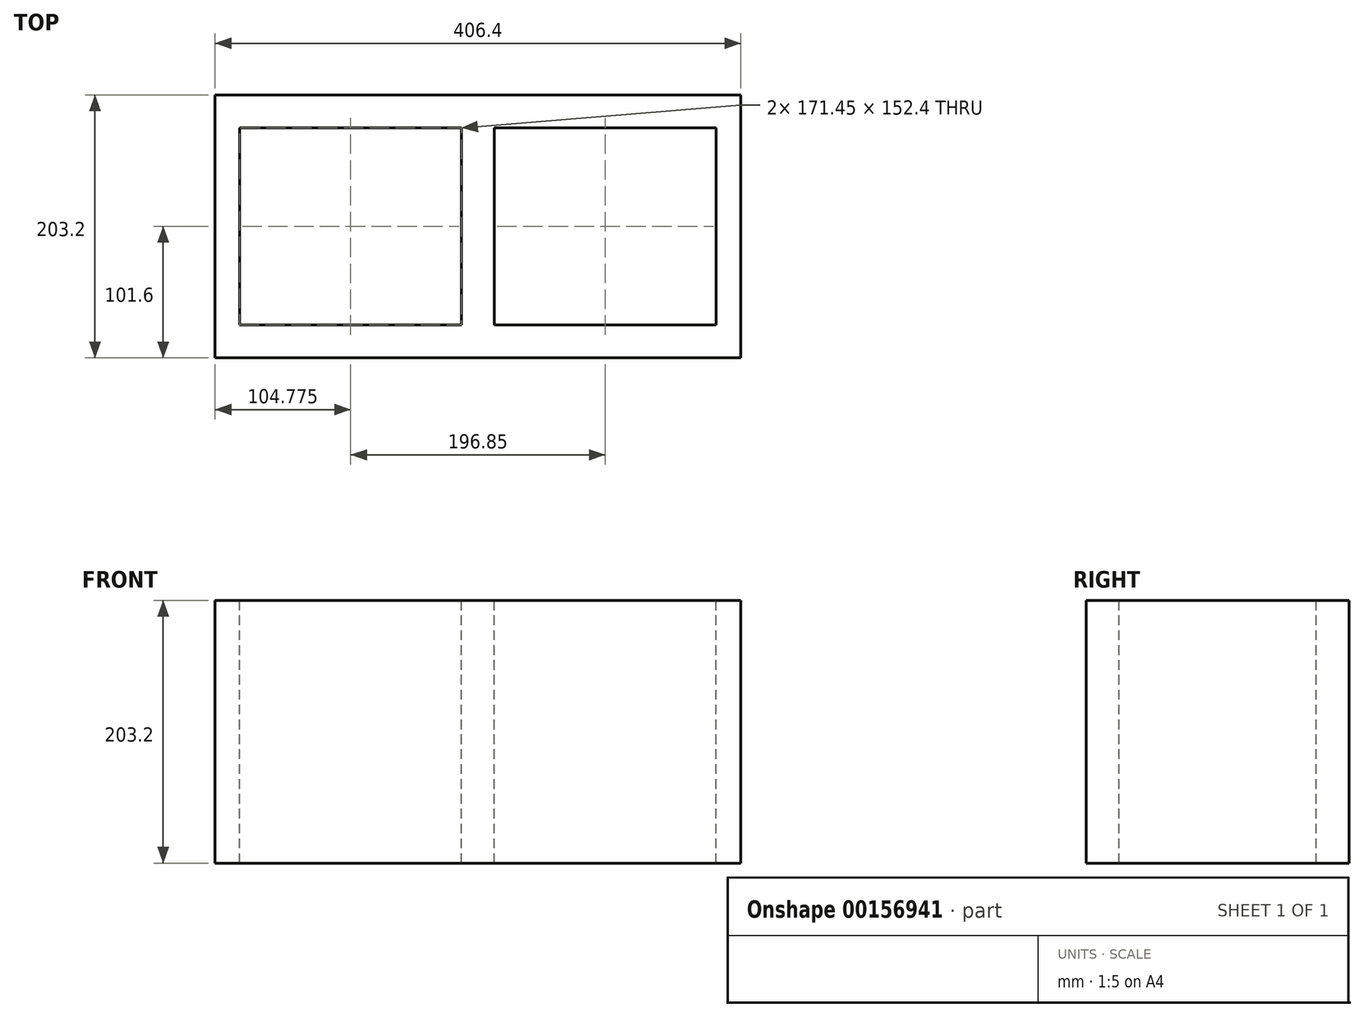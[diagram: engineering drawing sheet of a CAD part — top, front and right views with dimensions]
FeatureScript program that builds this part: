
annotation { "Feature Type Name" : "Feature", "Feature Type Description" : "" }
export const myFeature = defineFeature(function(context is Context, id is Id, definition is map)
    precondition{}
    {
        {
            var Q0;
            Q0=qCreatedBy(makeId("Front.planeOp"),FACE);
            var sketch = newSketch(context, id + "F0", { "sketchPlane" : qUnion([Q0])});
            skLineSegment(sketch, "E0.bottom", {"start": v(-406.4, -203.2) * mm, "end": v(0, -203.2) * mm});
            skLineSegment(sketch, "E0.top", {"start": v(-406.4, 0) * mm, "end": v(0, 0) * mm});
            skLineSegment(sketch, "E0.left", {"start": v(-406.4, -203.2) * mm, "end": v(-406.4, 0) * mm});
            skLineSegment(sketch, "E0.right", {"start": v(0, -203.2) * mm, "end": v(0, 0) * mm});
            skSolve(sketch);
        }
        {
            var Q0;
            Q0=makeQuery(id+"F0.imprint","IMPRINT",FACE,{"disambiguationData":[TD([[makeQuery(id+"F0.imprint","IMPRINT",EDGE,{"derivedFrom":sQuery(id+"F0.wireOp",EDGE,"E0.bottom")}),1.0]])]});
            extrude(context, id + "F1", {"entities" : qUnion([Q0]), "depth" : 203.2 * mm});
        }
        {
            var Q0;
            Q0=makeQuery(id+"F1.opExtrude","SWEPT_FACE",FACE,{"disambiguationData":[OSD([sQuery(id+"F0.wireOp",EDGE,"E0.top")])]});
            var sketch = newSketch(context, id + "F2", { "sketchPlane" : qUnion([Q0])});
            skLineSegment(sketch, "E1.bottom", {"start": v(-387.35, -25.4) * mm, "end": v(-215.9, -25.4) * mm});
            skLineSegment(sketch, "E1.top", {"start": v(-387.35, -177.8) * mm, "end": v(-215.9, -177.8) * mm});
            skLineSegment(sketch, "E1.left", {"start": v(-387.35, -25.4) * mm, "end": v(-387.35, -177.8) * mm});
            skLineSegment(sketch, "E1.right", {"start": v(-215.9, -25.4) * mm, "end": v(-215.9, -177.8) * mm});
            skLineSegment(sketch, "E2.bottom", {"start": v(-190.5, -25.4) * mm, "end": v(-19.05, -25.4) * mm});
            skLineSegment(sketch, "E2.top", {"start": v(-190.5, -177.8) * mm, "end": v(-19.05, -177.8) * mm});
            skLineSegment(sketch, "E2.left", {"start": v(-190.5, -25.4) * mm, "end": v(-190.5, -177.8) * mm});
            skLineSegment(sketch, "E2.right", {"start": v(-19.05, -25.4) * mm, "end": v(-19.05, -177.8) * mm});
            skSolve(sketch);
        }
        {
            var Q0;
            Q0=makeQuery(id+"F2.imprint","IMPRINT",FACE,{"disambiguationData":[TD([[makeQuery(id+"F2.imprint","IMPRINT",EDGE,{"derivedFrom":sQuery(id+"F2.wireOp",EDGE,"E1.bottom")}),-1.0]])]});
            var Q1;
            Q1=makeQuery(id+"F2.imprint","IMPRINT",FACE,{"disambiguationData":[TD([[makeQuery(id+"F2.imprint","IMPRINT",EDGE,{"derivedFrom":sQuery(id+"F2.wireOp",EDGE,"E2.bottom")}),-1.0]])]});
            extrude(context, id + "F3", {"entities" : qUnion([Q0, Q1]), "operationType" : NewBodyOperationType.REMOVE, "endBound" : BoundingType.THROUGH_ALL, "oppositeDirection" : true, "depth" : 25.4 * mm});
        }
    });
